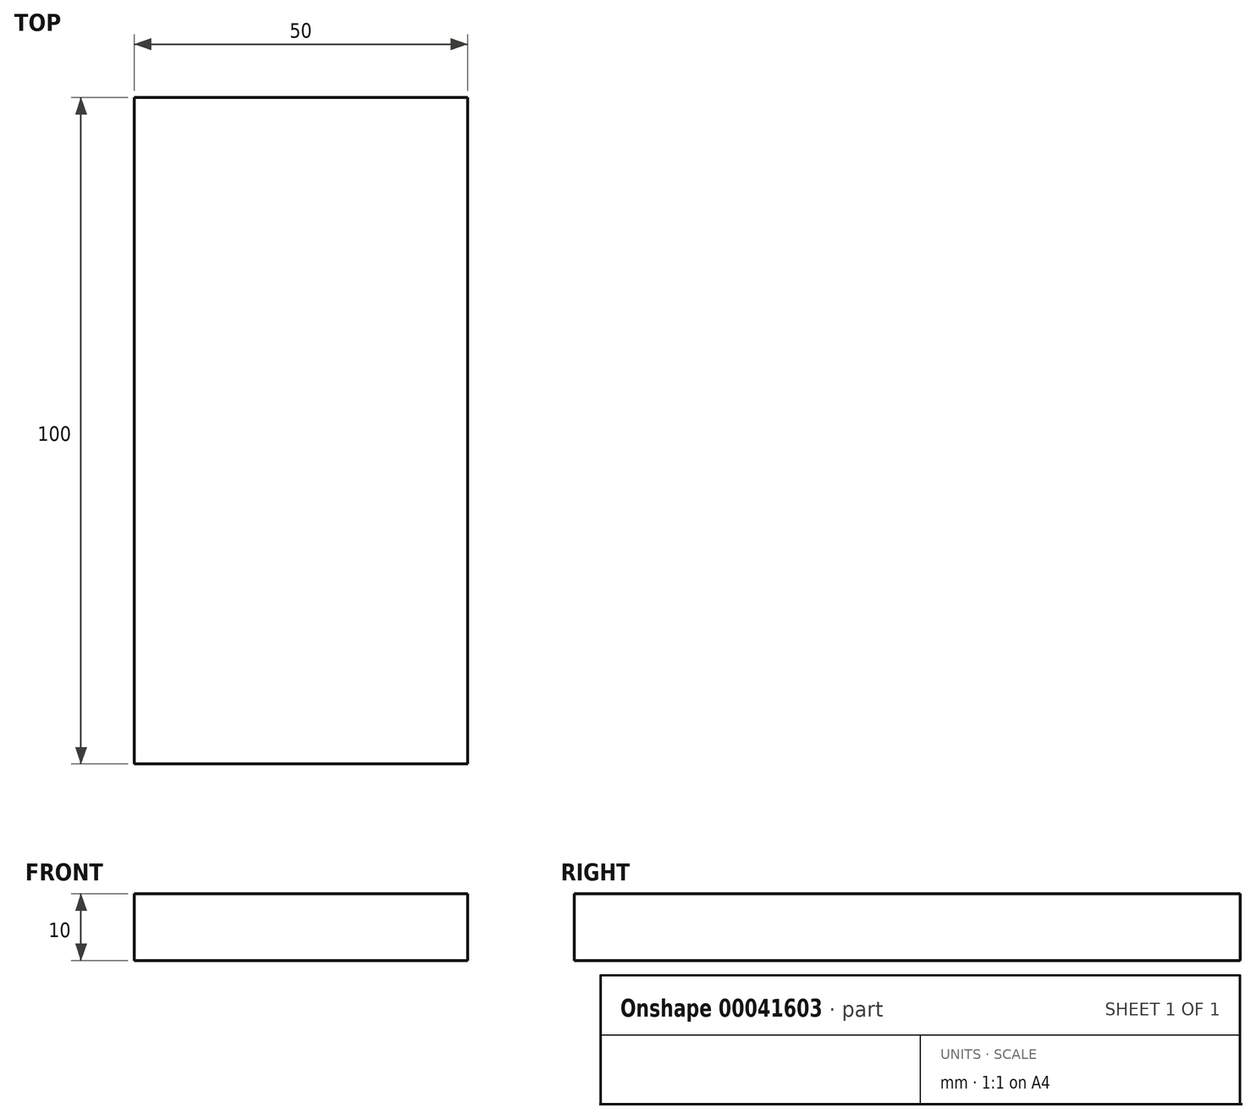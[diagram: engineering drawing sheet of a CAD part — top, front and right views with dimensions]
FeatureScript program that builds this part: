
annotation { "Feature Type Name" : "Feature", "Feature Type Description" : "" }
export const myFeature = defineFeature(function(context is Context, id is Id, definition is map)
    precondition{}
    {
        {
            var Q0;
            Q0=qCreatedBy(makeId("Top.planeOp"),FACE);
            var sketch = newSketch(context, id + "F0", { "sketchPlane" : qUnion([Q0])});
            skLineSegment(sketch, "E0.rect.bottom", {"start": v(-25, 50) * mm, "end": v(25, 50) * mm});
            skLineSegment(sketch, "E0.rect.top", {"start": v(-25, -50) * mm, "end": v(25, -50) * mm});
            skLineSegment(sketch, "E0.rect.left", {"start": v(-25, 50) * mm, "end": v(-25, -50) * mm});
            skLineSegment(sketch, "E0.rect.right", {"start": v(25, 50) * mm, "end": v(25, -50) * mm});
            skPoint(sketch, "E0.rect.middle", {"position": v(0, 0) * mm});
            skSolve(sketch);
        }
        {
            var Q0;
            Q0=makeQuery(id+"F0.imprint","IMPRINT",FACE,{"disambiguationData":[TD([[makeQuery(id+"F0.imprint","IMPRINT",EDGE,{"derivedFrom":sQuery(id+"F0.wireOp",EDGE,"E0.rect.bottom")}),-1.0]])]});
            extrude(context, id + "F1", {"entities" : qUnion([Q0]), "depth" : 10 * mm});
        }
    });
